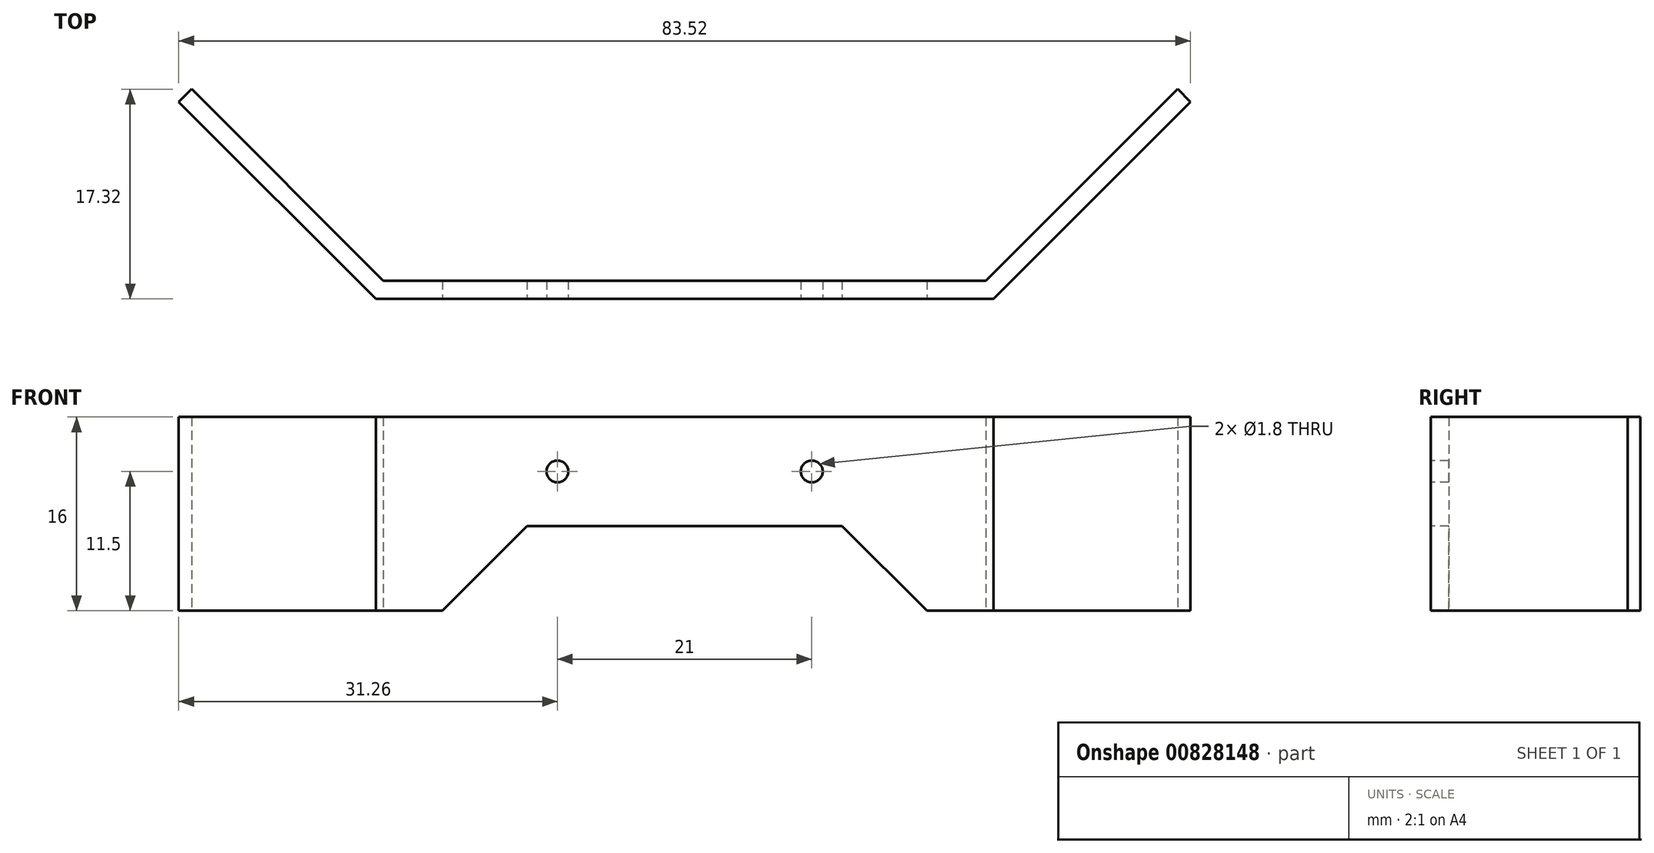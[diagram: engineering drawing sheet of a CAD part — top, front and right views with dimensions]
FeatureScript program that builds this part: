
annotation { "Feature Type Name" : "Feature", "Feature Type Description" : "" }
export const myFeature = defineFeature(function(context is Context, id is Id, definition is map)
    precondition{}
    {
        {
            var Q0;
            Q0=qCreatedBy(makeId("Top.planeOp"),FACE);
            var sketch = newSketch(context, id + "F0", { "sketchPlane" : qUnion([Q0])});
            skLineSegment(sketch, "E0", {"start": v(0, 0) * mm, "end": v(25.5, 0) * mm});
            skLineSegment(sketch, "E1", {"start": v(25.5, 0) * mm, "end": v(41.76, 16.26) * mm});
            skLineSegment(sketch, "E2", {"start": v(41.76, 16.26) * mm, "end": v(40.7, 17.32) * mm});
            skLineSegment(sketch, "E3", {"start": v(40.7, 17.32) * mm, "end": v(24.88, 1.5) * mm});
            skLineSegment(sketch, "E4", {"start": v(24.88, 1.5) * mm, "end": v(0, 1.5) * mm});
            skLineSegment(sketch, "E5", {"start": v(0, 0) * mm, "end": v(0, 34.97) * mm, "construction": true});
            skLineSegment(sketch, "E6.MirrorCS", {"start": v(-41.76, 16.26) * mm, "end": v(-40.7, 17.32) * mm});
            skLineSegment(sketch, "E7.MirrorCS", {"start": v(-24.88, 1.5) * mm, "end": v(0, 1.5) * mm});
            skLineSegment(sketch, "E8.MirrorCS", {"start": v(0, 0) * mm, "end": v(-25.5, 0) * mm});
            skLineSegment(sketch, "E9.MirrorCS", {"start": v(-25.5, 0) * mm, "end": v(-41.76, 16.26) * mm});
            skLineSegment(sketch, "E10.MirrorCS", {"start": v(-40.7, 17.32) * mm, "end": v(-24.88, 1.5) * mm});
            skSolve(sketch);
        }
        {
            var Q0;
            Q0 = qSketchRegion(id + "F0", true);
            extrude(context, id + "F1", {"entities" : qUnion([Q0]), "depth" : 16 * mm, "offsetDistance" : 25 * mm});
        }
        {
            var Q0;
            Q0=makeQuery(id+"F1.opExtrude","SWEPT_FACE",FACE,{"disambiguationData":[OSD([sQuery(id+"F0.wireOp",EDGE,"E0"),sQuery(id+"F0.wireOp",EDGE,"E8.MirrorCS")])]});
            var sketch = newSketch(context, id + "F2", { "sketchPlane" : qUnion([Q0])});
            skCircle(sketch, "E11", {"center": v(-10.5, 11.5) * mm, "radius": 0.9 * mm});
            skCircle(sketch, "E12", {"center": v(10.5, 11.5) * mm, "radius": 0.9 * mm});
            skLineSegment(sketch, "E13", {"start": v(-20, 0) * mm, "end": v(-13, 7) * mm});
            skLineSegment(sketch, "E14", {"start": v(-13, 7) * mm, "end": v(13, 7) * mm});
            skLineSegment(sketch, "E15", {"start": v(13, 7) * mm, "end": v(20, 0) * mm});
            skLineSegment(sketch, "E16", {"start": v(20, 0) * mm, "end": v(-20, 0) * mm});
            skSolve(sketch);
        }
        {
            var Q0;
            Q0 = qSketchRegion(id + "F2", true);
            extrude(context, id + "F3", {"entities" : qUnion([Q0]), "operationType" : NewBodyOperationType.REMOVE, "endBound" : BoundingType.THROUGH_ALL, "oppositeDirection" : true, "depth" : 25 * mm, "offsetDistance" : 25 * mm});
        }
    });
